# Revit family: 208_SGR-0-_-_
name_source: partatom
category: Air Terminals
units: mm (PartAtom-declared; Revit-internal decimal feet)

## family parameters
Always vertical = Yes
Cut with Voids When Loaded = No
Part Type = Normal
Room Calculation Point = Yes
Round Connector Dimension = Use Diameter
Shared = No
Work Plane-Based = No

## types (14) — shared parameters
A1 = 5 mm  [stored 0.0164042 ft]
CAT0 = Yes
CL_Location_5000 = 5000 mm  [stored 16.4042 ft]
Description = GRILLE FOR ROUND DUCT WITH SINGLE BARS
L_ARR = 400 mm  [stored 1.31234 ft]
Manufacturer = Alnor
URL = http://www.ventilation-alnor.co.uk
W_ARR = 400 mm  [stored 1.31234 ft]
XRefLineVPlnId = 7453
YRefLineVPlnId = 7456
magiPartTypeId = 208
magiProductFamilyId = SGR-0-*-*
zero-valued in all types: CLBTZ, H_ARR

## per-type parameters (varying)
| type | B | H | H1 | H11 | L11 | magiProductId |
| SGR 0 325 75 | 325 mm | 75 mm | 125 mm  [stored 0.410105 ft] | 63 mm | 183 mm | SGR-0-325-75 |
| SGR 0 825 225 | 825 mm | 225 mm | 275 mm | 138 mm | 433 mm | SGR-0-825-225 |
| SGR 0 625 225 | 625 mm | 225 mm | 275 mm | 138 mm | 333 mm | SGR-0-625-225 |
| SGR 0 525 225 | 525 mm | 225 mm | 275 mm | 138 mm | 283 mm | SGR-0-525-225 |
| SGR 0 425 225 | 425 mm | 225 mm | 275 mm | 138 mm | 233 mm | SGR-0-425-225 |
| SGR 0 825 125 | 825 mm | 125 mm | 175 mm | 88 mm | 433 mm | SGR-0-825-125 |
| SGR 0 625 125 | 625 mm | 125 mm | 175 mm | 88 mm | 333 mm | SGR-0-625-125 |
| SGR 0 525 125 | 525 mm | 125 mm | 175 mm | 88 mm | 283 mm | SGR-0-525-125 |
| SGR 0 425 125 | 425 mm | 125 mm | 175 mm | 88 mm | 233 mm | SGR-0-425-125 |
| SGR 0 325 125 | 325 mm | 125 mm | 175 mm | 88 mm | 183 mm | SGR-0-325-125 |
| SGR 0 825 75 | 825 mm | 75 mm | 125 mm  [stored 0.410105 ft] | 63 mm | 433 mm | SGR-0-825-75 |
| SGR 0 625 75 | 625 mm | 75 mm | 125 mm  [stored 0.410105 ft] | 63 mm | 333 mm | SGR-0-625-75 |
| SGR 0 525 75 | 525 mm | 75 mm | 125 mm  [stored 0.410105 ft] | 63 mm | 283 mm | SGR-0-525-75 |
| SGR 0 425 75 | 425 mm | 75 mm | 125 mm  [stored 0.410105 ft] | 63 mm | 233 mm | SGR-0-425-75 |

note: column(s) folded — value = type name in every type: MC Product Code

note: [stored X ft] marks values corroborated as IEEE doubles in the binary element streams (Revit-internal decimal feet)

## geometry (parser evidence)
native form markers: Blend x4, Sweep x1
no freeform markers — native parametric forms only
